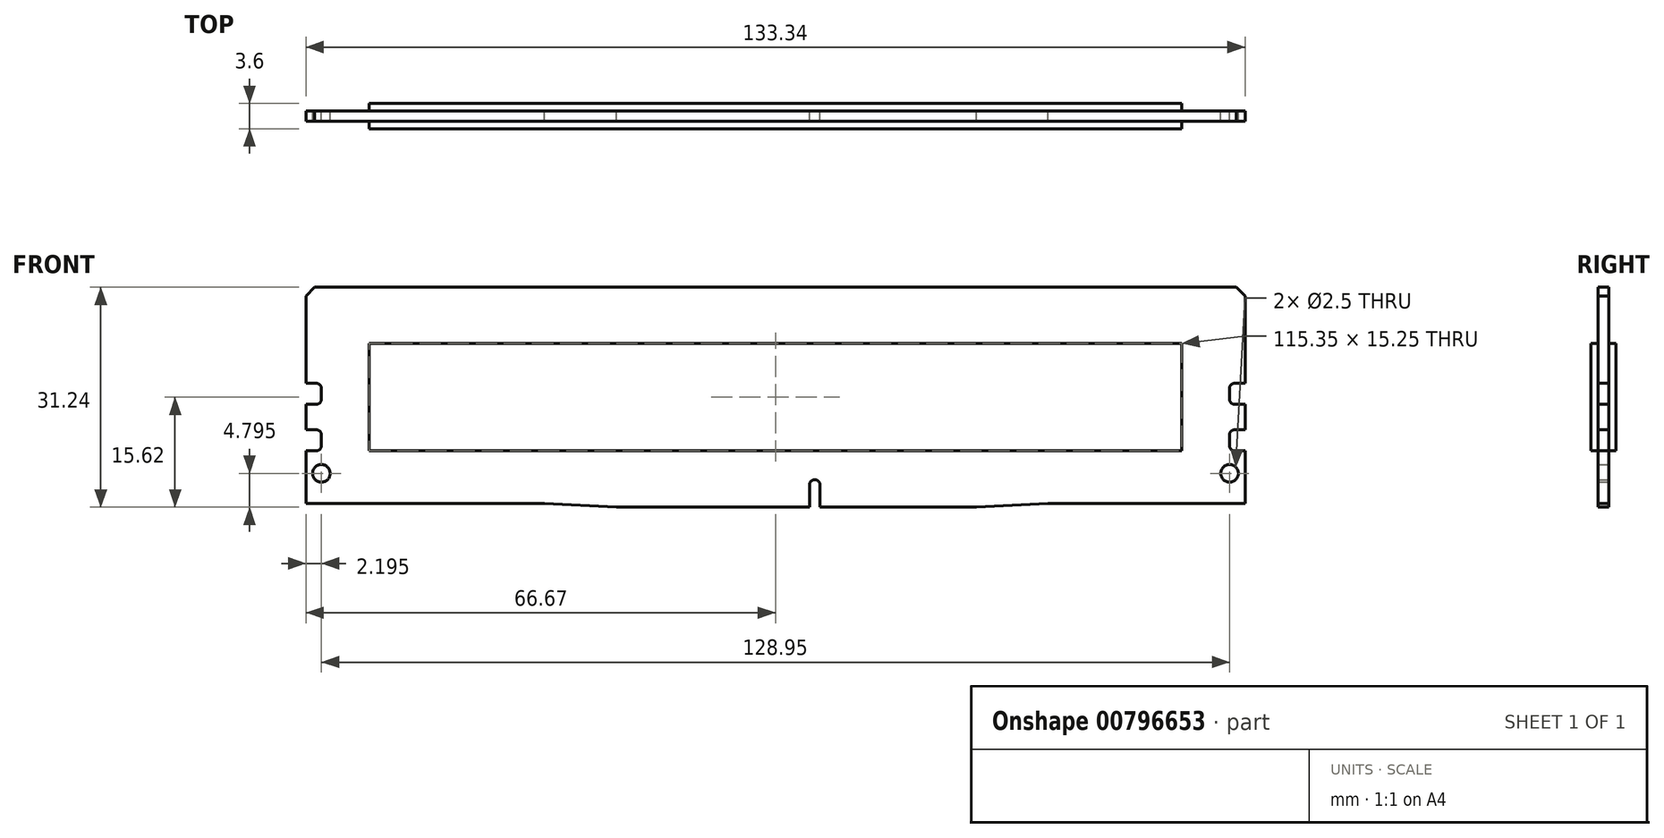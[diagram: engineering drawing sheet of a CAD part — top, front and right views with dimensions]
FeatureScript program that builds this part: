
annotation { "Feature Type Name" : "Feature", "Feature Type Description" : "" }
export const myFeature = defineFeature(function(context is Context, id is Id, definition is map)
    precondition{}
    {
        {
            var Q0;
            Q0=qCreatedBy(makeId("Front.planeOp"),FACE);
            var sketch = newSketch(context, id + "F0", { "sketchPlane" : qUnion([Q0])});
            skLineSegment(sketch, "E0.left", {"start": v(-66.67, -15.62) * mm, "end": v(-66.67, 15.62) * mm});
            skLineSegment(sketch, "E1", {"start": v(0, -15.63) * mm, "end": v(0, 15.62) * mm, "construction": true});
            skLineSegment(sketch, "E2", {"start": v(-66.68, 1.98) * mm, "end": v(-65.22, 1.98) * mm});
            skLineSegment(sketch, "E3", {"start": v(-64.47, 1.23) * mm, "end": v(-64.47, -0.27) * mm});
            skLineSegment(sketch, "E4", {"start": v(-65.22, -7.62) * mm, "end": v(-66.68, -7.62) * mm});
            skLineSegment(sketch, "E5", {"start": v(-66.68, -4.62) * mm, "end": v(-65.22, -4.62) * mm});
            skLineSegment(sketch, "E6", {"start": v(-66.68, -1.02) * mm, "end": v(-65.22, -1.02) * mm});
            skLineSegment(sketch, "E7.trimOffspring", {"start": v(-64.47, -5.37) * mm, "end": v(-64.47, -6.87) * mm});
            skPoint(sketch, "E8.visualSharp", {"position": v(-64.47, 1.98) * mm});
            skArc(sketch, "E8.filletArc", {"start": v(-64.47, 1.23) * mm, "mid": v(-64.7, 1.76) * mm, "end": v(-65.22, 1.98) * mm});
            skPoint(sketch, "E9.visualSharp", {"position": v(-64.47, -1.02) * mm});
            skArc(sketch, "E9.filletArc", {"start": v(-65.22, -1.02) * mm, "mid": v(-64.7, -0.8) * mm, "end": v(-64.47, -0.27) * mm});
            skPoint(sketch, "E10.visualSharp", {"position": v(-64.47, -4.63) * mm});
            skArc(sketch, "E10.filletArc", {"start": v(-64.47, -5.37) * mm, "mid": v(-64.7, -4.84) * mm, "end": v(-65.22, -4.62) * mm});
            skPoint(sketch, "E11.visualSharp", {"position": v(-64.47, -7.62) * mm});
            skArc(sketch, "E11.filletArc", {"start": v(-65.22, -7.62) * mm, "mid": v(-64.7, -7.4) * mm, "end": v(-64.47, -6.87) * mm});
            skPoint(sketch, "E12", {"position": v(-64.47, 0.48) * mm});
            skPoint(sketch, "E13", {"position": v(-64.48, -6.12) * mm});
            skArc(sketch, "E14.MirrorCS", {"start": v(65.22, -1.02) * mm, "mid": v(64.7, -0.8) * mm, "end": v(64.47, -0.27) * mm});
            skArc(sketch, "E15.MirrorCS", {"start": v(64.47, 1.22) * mm, "mid": v(64.7, 1.76) * mm, "end": v(65.22, 1.97) * mm});
            skArc(sketch, "E16.MirrorCS", {"start": v(64.47, -5.37) * mm, "mid": v(64.7, -4.84) * mm, "end": v(65.22, -4.62) * mm});
            skArc(sketch, "E17.MirrorCS", {"start": v(65.22, -7.62) * mm, "mid": v(64.7, -7.4) * mm, "end": v(64.47, -6.87) * mm});
            skLineSegment(sketch, "E18.MirrorCS", {"start": v(64.47, -5.37) * mm, "end": v(64.47, -6.87) * mm});
            skLineSegment(sketch, "E19.MirrorCS", {"start": v(64.47, 1.22) * mm, "end": v(64.47, -0.27) * mm});
            skLineSegment(sketch, "E20.MirrorCS", {"start": v(66.68, -1.02) * mm, "end": v(65.22, -1.02) * mm});
            skPoint(sketch, "E21.MirrorP", {"position": v(64.47, 0.48) * mm});
            skLineSegment(sketch, "E22.MirrorCS", {"start": v(66.68, -4.63) * mm, "end": v(65.22, -4.63) * mm});
            skLineSegment(sketch, "E23.MirrorCS", {"start": v(65.22, -7.62) * mm, "end": v(66.68, -7.62) * mm});
            skLineSegment(sketch, "E24.MirrorCS", {"start": v(66.68, -15.62) * mm, "end": v(66.68, 15.62) * mm});
            skLineSegment(sketch, "E25.MirrorCS", {"start": v(66.68, 1.98) * mm, "end": v(65.22, 1.98) * mm});
            skPoint(sketch, "E26.MirrorP", {"position": v(64.47, -7.62) * mm});
            skPoint(sketch, "E27.MirrorP", {"position": v(64.48, -6.12) * mm});
            skPoint(sketch, "E28.MirrorP", {"position": v(64.47, -4.63) * mm});
            skPoint(sketch, "E29.MirrorP", {"position": v(64.47, 1.98) * mm});
            skPoint(sketch, "E30.MirrorP", {"position": v(64.47, -1.02) * mm});
            skLineSegment(sketch, "E31", {"start": v(66.68, 15.62) * mm, "end": v(-66.68, 15.62) * mm});
            skLineSegment(sketch, "E32", {"start": v(66.68, -15.63) * mm, "end": v(-66.68, -15.63) * mm});
            skLineSegment(sketch, "E33", {"start": v(-66.68, 14.37) * mm, "end": v(-65.42, 15.62) * mm});
            skLineSegment(sketch, "E34.MirrorCS", {"start": v(66.67, 14.37) * mm, "end": v(65.42, 15.62) * mm});
            skLineSegment(sketch, "E35.bottom", {"start": v(4.82, -15.63) * mm, "end": v(6.32, -15.63) * mm});
            skLineSegment(sketch, "E35.left", {"start": v(4.82, -15.63) * mm, "end": v(4.82, -12.48) * mm});
            skLineSegment(sketch, "E35.right", {"start": v(6.32, -15.63) * mm, "end": v(6.32, -12.48) * mm});
            skArc(sketch, "E36", {"start": v(4.82, -12.48) * mm, "mid": v(5.57, -11.73) * mm, "end": v(6.32, -12.48) * mm});
            skCircle(sketch, "E37", {"center": v(-64.47, -10.83) * mm, "radius": 1.25 * mm});
            skCircle(sketch, "E38.MirrorC", {"center": v(64.47, -10.83) * mm, "radius": 1.25 * mm});
            skLineSegment(sketch, "E39", {"start": v(-66.67, -15.13) * mm, "end": v(-32.77, -15.13) * mm});
            skLineSegment(sketch, "E40", {"start": v(-32.77, -15.13) * mm, "end": v(-22.57, -15.63) * mm});
            skLineSegment(sketch, "E41", {"start": v(66.68, -15.13) * mm, "end": v(38.72, -15.13) * mm});
            skLineSegment(sketch, "E42", {"start": v(38.72, -15.13) * mm, "end": v(28.52, -15.63) * mm});
            skPoint(sketch, "E43", {"position": v(0, 15.62) * mm});
            skSolve(sketch);
        }
        {
            var Q0;
            {var subQ2=sQuery(id+"F0.wireOp",EDGE,"E2");Q0=makeQuery(id+"F0.imprint","IMPRINT",FACE,{"disambiguationData":[TD([[makeQuery(id+"F0.imprint","IMPRINT",EDGE,{"derivedFrom":subQ2}),1.0]])]});}
            extrude(context, id + "F1", {"entities" : qUnion([Q0]), "endBound" : BoundingType.SYMMETRIC, "depth" : 1.5 * mm, "offsetDistance" : 25.4 * mm});
        }
        {
            var Q0;
            Q0=qCreatedBy(makeId("Front.planeOp"),FACE);
            var sketch = newSketch(context, id + "F2", { "sketchPlane" : qUnion([Q0])});
            skLineSegment(sketch, "E44.bottom", {"start": v(-57.67, -7.63) * mm, "end": v(57.68, -7.63) * mm});
            skLineSegment(sketch, "E44.top", {"start": v(-57.67, 7.62) * mm, "end": v(57.68, 7.62) * mm});
            skLineSegment(sketch, "E44.left", {"start": v(-57.67, -7.63) * mm, "end": v(-57.67, 7.62) * mm});
            skLineSegment(sketch, "E44.right", {"start": v(57.68, -7.63) * mm, "end": v(57.68, 7.62) * mm});
            skSolve(sketch);
        }
        {
            var Q0;
            Q0=makeQuery(id+"F2.imprint","IMPRINT",FACE,{"disambiguationData":[TD([[makeQuery(id+"F2.imprint","IMPRINT",EDGE,{"derivedFrom":sQuery(id+"F2.wireOp",EDGE,"E44.bottom")}),1.0]])]});
            extrude(context, id + "F3", {"entities" : qUnion([Q0]), "operationType" : NewBodyOperationType.ADD, "endBound" : BoundingType.SYMMETRIC, "depth" : 3.6 * mm, "offsetDistance" : 25 * mm});
        }
    });
